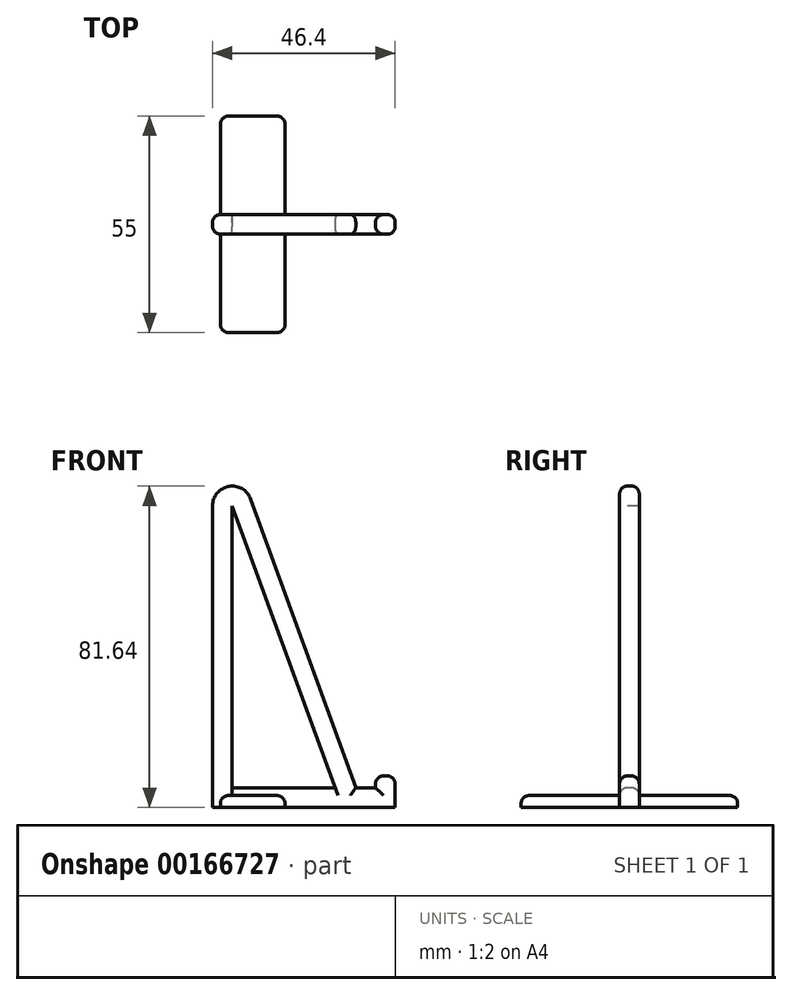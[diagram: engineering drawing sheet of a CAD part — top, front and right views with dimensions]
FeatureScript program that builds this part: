
annotation { "Feature Type Name" : "Feature", "Feature Type Description" : "" }
export const myFeature = defineFeature(function(context is Context, id is Id, definition is map)
    precondition{}
    {
        {
            var Q0;
            Q0=qCreatedBy(makeId("Front.planeOp"),FACE);
            var sketch = newSketch(context, id + "F0", { "sketchPlane" : qUnion([Q0])});
            skLineSegment(sketch, "E0", {"start": v(0, 0) * mm, "end": v(-46.4, 0) * mm});
            skLineSegment(sketch, "E1", {"start": v(-46.4, 0) * mm, "end": v(-46.4, 105) * mm});
            skLineSegment(sketch, "E2", {"start": v(-46.4, 105) * mm, "end": v(-10, 5) * mm});
            skLineSegment(sketch, "E3", {"start": v(-10, 5) * mm, "end": v(-5, 5) * mm});
            skLineSegment(sketch, "E4", {"start": v(-5, 5) * mm, "end": v(-5, 8) * mm});
            skLineSegment(sketch, "E5", {"start": v(-5, 8) * mm, "end": v(0, 8) * mm});
            skLineSegment(sketch, "E6", {"start": v(0, 8) * mm, "end": v(0, 0) * mm});
            skLineSegment(sketch, "E7", {"start": v(-41.4, 76.64) * mm, "end": v(-41.4, 5) * mm});
            skLineSegment(sketch, "E8", {"start": v(-41.4, 5) * mm, "end": v(-15.32, 5) * mm});
            skLineSegment(sketch, "E9", {"start": v(-15.32, 5) * mm, "end": v(-41.4, 76.64) * mm});
            skSolve(sketch);
        }
        {
            var Q0;
            Q0=makeQuery(id+"F0.imprint","IMPRINT",FACE,{"disambiguationData":[TD([[makeQuery(id+"F0.imprint","IMPRINT",EDGE,{"derivedFrom":sQuery(id+"F0.wireOp",EDGE,"E0")}),-1.0]])]});
            extrude(context, id + "F1", {"entities" : qUnion([Q0]), "oppositeDirection" : true, "depth" : 5 * mm});
        }
        {
            var Q0;
            Q0=makeQuery(id+"F1.opExtrude","SWEPT_FACE",FACE,{"disambiguationData":[OSD([sQuery(id+"F0.wireOp",EDGE,"E1")])]});
            var sketch = newSketch(context, id + "F2", { "sketchPlane" : qUnion([Q0])});
            skLineSegment(sketch, "E10.bottom", {"start": v(-5, 105) * mm, "end": v(0, 105) * mm});
            skLineSegment(sketch, "E10.top", {"start": v(-5, 5) * mm, "end": v(0, 5) * mm});
            skLineSegment(sketch, "E10.left", {"start": v(0, 105) * mm, "end": v(0, 5) * mm});
            skLineSegment(sketch, "E10.right", {"start": v(-5, 105) * mm, "end": v(-5, 5) * mm});
            skSolve(sketch);
        }
        {
            var Q0;
            Q0=makeQuery(id+"F9Pola5RWQbzexP_1.boolean.opBoolean","MERGE",FACE,{"derivedFrom":[makeQuery(id+"F1.opExtrude","SWEPT_FACE",FACE,{"disambiguationData":[OSD([sQuery(id+"F0.wireOp",EDGE,"E3")])]}),makeQuery(id+"F1.opExtrude","SWEPT_FACE",FACE,{"disambiguationData":[OSD([sQuery(id+"F0.wireOp",EDGE,"E8")])]}),makeQuery(id+"F9Pola5RWQbzexP_1.opExtrude","SWEPT_FACE",FACE,{"disambiguationData":[OSD([sQuery(id+"F2.wireOp",EDGE,"E10.top")])]})]});
            var sketch = newSketch(context, id + "F3", { "sketchPlane" : qUnion([Q0])});
            skLineSegment(sketch, "E11.bottom", {"start": v(0, 185) * mm, "end": v(-10, 185) * mm});
            skLineSegment(sketch, "E11.top", {"start": v(0, 5) * mm, "end": v(-10, 5) * mm});
            skLineSegment(sketch, "E11.left", {"start": v(0, 185) * mm, "end": v(0, 5) * mm});
            skLineSegment(sketch, "E11.right", {"start": v(-10, 185) * mm, "end": v(-10, 5) * mm});
            skSolve(sketch);
        }
        {
            var Q0;
            {var subQ0=sQuery(id+"F3.wireOp",EDGE,"E11.left");Q0=makeQuery(id+"F3.imprint","IMPRINT",FACE,{"disambiguationData":[TD([[makeQuery(id+"F3.imprint","IMPRINT",EDGE,{"derivedFrom":subQ0}),-1.0]])]});}
            extrude(context, id + "F4", {"entities" : qUnion([Q0]), "operationType" : NewBodyOperationType.REMOVE, "endBound" : BoundingType.THROUGH_ALL, "oppositeDirection" : true, "depth" : 25 * mm});
        }
        {
            var Q0;
            {var subQ0=sQuery(id+"F0.wireOp",EDGE,"E2");var subQ1=sQuery(id+"F0.wireOp",EDGE,"E1");Q0=makeQuery(id+"F9Pola5RWQbzexP_1.boolean.opBoolean","SPLIT",EDGE,{"disambiguationData":[TD([makeQuery(id+"F9Pola5RWQbzexP_1.opExtrude","SWEPT_FACE",FACE,{"disambiguationData":[OSD([sQuery(id+"F2.wireOp",EDGE,"E10.right")])]})])],"derivedFrom":makeQuery(id+"F1.opExtrude","SWEPT_EDGE",EDGE,{"disambiguationData":[OSD([subQ1,subQ0])]})});}
            var Q1;
            {var subQ0=sQuery(id+"F0.wireOp",EDGE,"E2");var subQ1=sQuery(id+"F0.wireOp",EDGE,"E1");Q1=makeQuery(id+"F9Pola5RWQbzexP_1.boolean.opBoolean","SPLIT",EDGE,{"disambiguationData":[TD([makeQuery(id+"F9Pola5RWQbzexP_1.opExtrude","SWEPT_FACE",FACE,{"disambiguationData":[OSD([sQuery(id+"F2.wireOp",EDGE,"E10.left")])]})])],"derivedFrom":makeQuery(id+"F1.opExtrude","SWEPT_EDGE",EDGE,{"disambiguationData":[OSD([subQ1,subQ0])]})});}
            fillet(context, id + "F5", {"entities" : qUnion([Q0, Q1]), "radius" : 5 * mm, "tangentPropagation" : true, "allowEdgeOverflow" : false});
        }
        {
            var Q0;
            {var subQ0=sQuery(id+"F0.wireOp",EDGE,"E9");var subQ1=sQuery(id+"F0.wireOp",EDGE,"E7");var subQ2=makeQuery(id+"F1.opExtrude","CAP_FACE",FACE,{"disambiguationData":[OSD([sQuery(id+"F0.wireOp",EDGE,"E0"),sQuery(id+"F0.wireOp",EDGE,"E1"),sQuery(id+"F0.wireOp",EDGE,"E2"),sQuery(id+"F0.wireOp",EDGE,"E3"),sQuery(id+"F0.wireOp",EDGE,"E4"),sQuery(id+"F0.wireOp",EDGE,"E5"),sQuery(id+"F0.wireOp",EDGE,"E6"),subQ1,sQuery(id+"F0.wireOp",EDGE,"E8"),subQ0])],"isStart":false});Q0=makeQuery(id+"F5.opFillet","BLEND_EDGE",EDGE,{"blendedFrom":[makeQuery(id+"F9Pola5RWQbzexP_1.boolean.opBoolean","SPLIT",EDGE,{"disambiguationData":[TD([makeQuery(id+"F9Pola5RWQbzexP_1.opExtrude","SWEPT_FACE",FACE,{"disambiguationData":[OSD([sQuery(id+"F2.wireOp",EDGE,"E10.left")])]})])],"derivedFrom":makeQuery(id+"F1.opExtrude","SWEPT_EDGE",EDGE,{"disambiguationData":[OSD([subQ1,subQ0])]})}),subQ2],"blendedInto":[subQ2]});}
            var Q1;
            {var subQ0=sQuery(id+"F0.wireOp",EDGE,"E2");var subQ1=sQuery(id+"F0.wireOp",EDGE,"E1");var subQ2=makeQuery(id+"F1.opExtrude","CAP_FACE",FACE,{"disambiguationData":[OSD([sQuery(id+"F0.wireOp",EDGE,"E0"),subQ1,subQ0,sQuery(id+"F0.wireOp",EDGE,"E3"),sQuery(id+"F0.wireOp",EDGE,"E4"),sQuery(id+"F0.wireOp",EDGE,"E5"),sQuery(id+"F0.wireOp",EDGE,"E6"),sQuery(id+"F0.wireOp",EDGE,"E7"),sQuery(id+"F0.wireOp",EDGE,"E8"),sQuery(id+"F0.wireOp",EDGE,"E9")])],"isStart":false});Q1=makeQuery(id+"F5.opFillet","BLEND_EDGE",EDGE,{"blendedFrom":[makeQuery(id+"F9Pola5RWQbzexP_1.boolean.opBoolean","SPLIT",EDGE,{"disambiguationData":[TD([makeQuery(id+"F9Pola5RWQbzexP_1.opExtrude","SWEPT_FACE",FACE,{"disambiguationData":[OSD([sQuery(id+"F2.wireOp",EDGE,"E10.left")])]})])],"derivedFrom":makeQuery(id+"F1.opExtrude","SWEPT_EDGE",EDGE,{"disambiguationData":[OSD([subQ1,subQ0])]})}),subQ2],"blendedInto":[subQ2]});}
            var Q2;
            {var subQ2=sQuery(id+"F0.wireOp",EDGE,"E7");var subQ4=sQuery(id+"F0.wireOp",EDGE,"E1");var subQ6=sQuery(id+"F0.wireOp",EDGE,"E9");var subQ8=makeQuery(id+"F9Pola5RWQbzexP_1.opExtrude","SWEPT_FACE",FACE,{"disambiguationData":[OSD([sQuery(id+"F2.wireOp",EDGE,"E10.right")])]});Q2=makeQuery(id+"F5.opFillet","BLEND_EDGE",EDGE,{"blendedFrom":[makeQuery(id+"F9Pola5RWQbzexP_1.boolean.opBoolean","SPLIT",EDGE,{"disambiguationData":[TD([subQ8])],"derivedFrom":makeQuery(id+"F1.opExtrude","SWEPT_EDGE",EDGE,{"disambiguationData":[OSD([subQ2,subQ6])]})}),makeQuery(id+"F9Pola5RWQbzexP_1.boolean.opBoolean","COPY",FACE,{"disambiguationData":[TD([makeQuery(id+"F1.opExtrude","SWEPT_FACE",FACE,{"disambiguationData":[OSD([subQ4])]})])],"derivedFrom":subQ8})],"blendedInto":[makeQuery(id+"F9Pola5RWQbzexP_1.boolean.opBoolean","COPY",FACE,{"disambiguationData":[TD([makeQuery(id+"F1.opExtrude","SWEPT_FACE",FACE,{"disambiguationData":[OSD([subQ4])]})])],"derivedFrom":subQ8})]});}
            var Q3;
            {var subQ1=sQuery(id+"F0.wireOp",EDGE,"E2");var subQ4=sQuery(id+"F0.wireOp",EDGE,"E1");var subQ5=makeQuery(id+"F1.opExtrude","SWEPT_FACE",FACE,{"disambiguationData":[OSD([subQ4])]});var subQ8=makeQuery(id+"F9Pola5RWQbzexP_1.opExtrude","SWEPT_FACE",FACE,{"disambiguationData":[OSD([sQuery(id+"F2.wireOp",EDGE,"E10.right")])]});Q3=makeQuery(id+"F5.opFillet","BLEND_EDGE",EDGE,{"blendedFrom":[makeQuery(id+"F9Pola5RWQbzexP_1.boolean.opBoolean","SPLIT",EDGE,{"disambiguationData":[TD([subQ8])],"derivedFrom":makeQuery(id+"F1.opExtrude","SWEPT_EDGE",EDGE,{"disambiguationData":[OSD([subQ4,subQ1])]})}),makeQuery(id+"F9Pola5RWQbzexP_1.boolean.opBoolean","COPY",FACE,{"disambiguationData":[TD([subQ5])],"derivedFrom":subQ8})],"blendedInto":[makeQuery(id+"F9Pola5RWQbzexP_1.boolean.opBoolean","COPY",FACE,{"disambiguationData":[TD([subQ5])],"derivedFrom":subQ8})]});}
            var Q4;
            {var subQ0=sQuery(id+"F0.wireOp",EDGE,"E9");var subQ1=sQuery(id+"F0.wireOp",EDGE,"E7");var subQ2=makeQuery(id+"F1.opExtrude","CAP_FACE",FACE,{"disambiguationData":[OSD([sQuery(id+"F0.wireOp",EDGE,"E0"),sQuery(id+"F0.wireOp",EDGE,"E1"),sQuery(id+"F0.wireOp",EDGE,"E2"),sQuery(id+"F0.wireOp",EDGE,"E3"),sQuery(id+"F0.wireOp",EDGE,"E4"),sQuery(id+"F0.wireOp",EDGE,"E5"),sQuery(id+"F0.wireOp",EDGE,"E6"),subQ1,sQuery(id+"F0.wireOp",EDGE,"E8"),subQ0])],"isStart":true});Q4=makeQuery(id+"F5.opFillet","BLEND_EDGE",EDGE,{"blendedFrom":[makeQuery(id+"F9Pola5RWQbzexP_1.boolean.opBoolean","SPLIT",EDGE,{"disambiguationData":[TD([makeQuery(id+"F9Pola5RWQbzexP_1.opExtrude","SWEPT_FACE",FACE,{"disambiguationData":[OSD([sQuery(id+"F2.wireOp",EDGE,"E10.right")])]})])],"derivedFrom":makeQuery(id+"F1.opExtrude","SWEPT_EDGE",EDGE,{"disambiguationData":[OSD([subQ1,subQ0])]})}),subQ2],"blendedInto":[subQ2]});}
            var Q5;
            {var subQ0=sQuery(id+"F0.wireOp",EDGE,"E2");var subQ1=sQuery(id+"F0.wireOp",EDGE,"E1");var subQ2=makeQuery(id+"F1.opExtrude","CAP_FACE",FACE,{"disambiguationData":[OSD([sQuery(id+"F0.wireOp",EDGE,"E0"),subQ1,subQ0,sQuery(id+"F0.wireOp",EDGE,"E3"),sQuery(id+"F0.wireOp",EDGE,"E4"),sQuery(id+"F0.wireOp",EDGE,"E5"),sQuery(id+"F0.wireOp",EDGE,"E6"),sQuery(id+"F0.wireOp",EDGE,"E7"),sQuery(id+"F0.wireOp",EDGE,"E8"),sQuery(id+"F0.wireOp",EDGE,"E9")])],"isStart":true});Q5=makeQuery(id+"F5.opFillet","BLEND_EDGE",EDGE,{"blendedFrom":[makeQuery(id+"F9Pola5RWQbzexP_1.boolean.opBoolean","SPLIT",EDGE,{"disambiguationData":[TD([makeQuery(id+"F9Pola5RWQbzexP_1.opExtrude","SWEPT_FACE",FACE,{"disambiguationData":[OSD([sQuery(id+"F2.wireOp",EDGE,"E10.right")])]})])],"derivedFrom":makeQuery(id+"F1.opExtrude","SWEPT_EDGE",EDGE,{"disambiguationData":[OSD([subQ1,subQ0])]})}),subQ2],"blendedInto":[subQ2]});}
            var Q6;
            {var subQ2=sQuery(id+"F0.wireOp",EDGE,"E7");var subQ4=sQuery(id+"F0.wireOp",EDGE,"E1");var subQ6=sQuery(id+"F0.wireOp",EDGE,"E9");var subQ8=makeQuery(id+"F9Pola5RWQbzexP_1.opExtrude","SWEPT_FACE",FACE,{"disambiguationData":[OSD([sQuery(id+"F2.wireOp",EDGE,"E10.left")])]});Q6=makeQuery(id+"F5.opFillet","BLEND_EDGE",EDGE,{"blendedFrom":[makeQuery(id+"F9Pola5RWQbzexP_1.boolean.opBoolean","SPLIT",EDGE,{"disambiguationData":[TD([subQ8])],"derivedFrom":makeQuery(id+"F1.opExtrude","SWEPT_EDGE",EDGE,{"disambiguationData":[OSD([subQ2,subQ6])]})}),makeQuery(id+"F9Pola5RWQbzexP_1.boolean.opBoolean","COPY",FACE,{"disambiguationData":[TD([makeQuery(id+"F1.opExtrude","SWEPT_FACE",FACE,{"disambiguationData":[OSD([subQ4])]})])],"derivedFrom":subQ8})],"blendedInto":[makeQuery(id+"F9Pola5RWQbzexP_1.boolean.opBoolean","COPY",FACE,{"disambiguationData":[TD([makeQuery(id+"F1.opExtrude","SWEPT_FACE",FACE,{"disambiguationData":[OSD([subQ4])]})])],"derivedFrom":subQ8})]});}
            var Q7;
            {var subQ1=sQuery(id+"F0.wireOp",EDGE,"E2");var subQ4=sQuery(id+"F0.wireOp",EDGE,"E1");var subQ5=makeQuery(id+"F1.opExtrude","SWEPT_FACE",FACE,{"disambiguationData":[OSD([subQ4])]});var subQ8=makeQuery(id+"F9Pola5RWQbzexP_1.opExtrude","SWEPT_FACE",FACE,{"disambiguationData":[OSD([sQuery(id+"F2.wireOp",EDGE,"E10.left")])]});Q7=makeQuery(id+"F5.opFillet","BLEND_EDGE",EDGE,{"blendedFrom":[makeQuery(id+"F9Pola5RWQbzexP_1.boolean.opBoolean","SPLIT",EDGE,{"disambiguationData":[TD([subQ8])],"derivedFrom":makeQuery(id+"F1.opExtrude","SWEPT_EDGE",EDGE,{"disambiguationData":[OSD([subQ4,subQ1])]})}),makeQuery(id+"F9Pola5RWQbzexP_1.boolean.opBoolean","COPY",FACE,{"disambiguationData":[TD([subQ5])],"derivedFrom":subQ8})],"blendedInto":[makeQuery(id+"F9Pola5RWQbzexP_1.boolean.opBoolean","COPY",FACE,{"disambiguationData":[TD([subQ5])],"derivedFrom":subQ8})]});}
            fillet(context, id + "F6", {"entities" : qUnion([Q0, Q1, Q2, Q3, Q4, Q5, Q6, Q7]), "radius" : 2 * mm, "tangentPropagation" : true, "allowEdgeOverflow" : false});
        }
        {
            var Q0;
            Q0=makeQuery(id+"F4.boolean.opBoolean","COPY",EDGE,{"derivedFrom":makeQuery(id+"F4.opExtrude","CAP_EDGE",EDGE,{"disambiguationData":[OSD([sQuery(id+"F3.wireOp",EDGE,"E11.right")])],"isStart":true})});
            var Q1;
            Q1=makeQuery(id+"F9Pola5RWQbzexP_1.boolean.opBoolean","COPY",EDGE,{"derivedFrom":makeQuery(id+"F9Pola5RWQbzexP_1.opExtrude","CAP_EDGE",EDGE,{"disambiguationData":[OSD([sQuery(id+"F2.wireOp",EDGE,"E10.top")])],"isStart":true})});
            var Q2;
            Q2=makeQuery(id+"F1.opExtrude","CAP_EDGE",EDGE,{"disambiguationData":[OSD([sQuery(id+"F0.wireOp",EDGE,"E8")])],"isStart":true});
            var Q3;
            Q3=makeQuery(id+"F1.opExtrude","CAP_EDGE",EDGE,{"disambiguationData":[OSD([sQuery(id+"F0.wireOp",EDGE,"E8")])],"isStart":false});
            fillet(context, id + "F7", {"entities" : qUnion([Q0, Q1, Q2, Q3]), "radius" : 2 * mm, "tangentPropagation" : true, "allowEdgeOverflow" : false});
        }
        {
            var Q0;
            {var subQ0=sQuery(id+"F0.wireOp",EDGE,"E6");var subQ1=sQuery(id+"F0.wireOp",EDGE,"E5");Q0=makeQuery(id+"F9Pola5RWQbzexP_1.boolean.opBoolean","SPLIT",EDGE,{"disambiguationData":[TD([makeQuery(id+"F9Pola5RWQbzexP_1.opExtrude","SWEPT_FACE",FACE,{"disambiguationData":[OSD([sQuery(id+"F2.wireOp",EDGE,"E10.right")])]})])],"derivedFrom":makeQuery(id+"F1.opExtrude","SWEPT_EDGE",EDGE,{"disambiguationData":[OSD([subQ1,subQ0])]})});}
            var Q1;
            Q1=makeQuery(id+"F9Pola5RWQbzexP_1.boolean.opBoolean","INTERSECT",EDGE,{"derivedFrom":[makeQuery(id+"F1.opExtrude","SWEPT_FACE",FACE,{"disambiguationData":[OSD([sQuery(id+"F0.wireOp",EDGE,"E5")])]}),makeQuery(id+"F9Pola5RWQbzexP_1.opExtrude","SWEPT_FACE",FACE,{"disambiguationData":[OSD([sQuery(id+"F2.wireOp",EDGE,"E10.right")])]})]});
            var Q2;
            Q2=makeQuery(id+"F1.opExtrude","CAP_EDGE",EDGE,{"disambiguationData":[OSD([sQuery(id+"F0.wireOp",EDGE,"E5")])],"isStart":true});
            var Q3;
            {var subQ0=sQuery(id+"F0.wireOp",EDGE,"E5");var subQ1=sQuery(id+"F0.wireOp",EDGE,"E4");Q3=makeQuery(id+"F9Pola5RWQbzexP_1.boolean.opBoolean","SPLIT",EDGE,{"disambiguationData":[TD([makeQuery(id+"F9Pola5RWQbzexP_1.opExtrude","SWEPT_FACE",FACE,{"disambiguationData":[OSD([sQuery(id+"F2.wireOp",EDGE,"E10.right")])]})])],"derivedFrom":makeQuery(id+"F1.opExtrude","SWEPT_EDGE",EDGE,{"disambiguationData":[OSD([subQ1,subQ0])]})});}
            var Q4;
            Q4=makeQuery(id+"F1.opExtrude","CAP_EDGE",EDGE,{"disambiguationData":[OSD([sQuery(id+"F0.wireOp",EDGE,"E4")])],"isStart":true});
            var Q5;
            Q5=makeQuery(id+"F1.opExtrude","CAP_EDGE",EDGE,{"disambiguationData":[OSD([sQuery(id+"F0.wireOp",EDGE,"E6")])],"isStart":true});
            var Q6;
            Q6=makeQuery(id+"F4.boolean.opBoolean","MERGE",EDGE,{"derivedFrom":[makeQuery(id+"F9Pola5RWQbzexP_1.boolean.opBoolean","INTERSECT",EDGE,{"derivedFrom":[makeQuery(id+"F1.opExtrude","SWEPT_FACE",FACE,{"disambiguationData":[OSD([sQuery(id+"F0.wireOp",EDGE,"E6")])]}),makeQuery(id+"F9Pola5RWQbzexP_1.opExtrude","SWEPT_FACE",FACE,{"disambiguationData":[OSD([sQuery(id+"F2.wireOp",EDGE,"E10.right")])]})]}),makeQuery(id+"F4.opExtrude","SWEPT_EDGE",EDGE,{"disambiguationData":[OSD([sQuery(id+"F3.wireOp",EDGE,"E11.top"),sQuery(id+"F3.wireOp",EDGE,"E11.left")])]})]});
            var Q7;
            Q7=makeQuery(id+"F9Pola5RWQbzexP_1.boolean.opBoolean","INTERSECT",EDGE,{"derivedFrom":[makeQuery(id+"F1.opExtrude","SWEPT_FACE",FACE,{"disambiguationData":[OSD([sQuery(id+"F0.wireOp",EDGE,"E4")])]}),makeQuery(id+"F9Pola5RWQbzexP_1.opExtrude","SWEPT_FACE",FACE,{"disambiguationData":[OSD([sQuery(id+"F2.wireOp",EDGE,"E10.right")])]})]});
            var Q8;
            Q8=makeQuery(id+"F4.boolean.opBoolean","COPY",EDGE,{"derivedFrom":makeQuery(id+"F4.opExtrude","CAP_EDGE",EDGE,{"disambiguationData":[OSD([sQuery(id+"F3.wireOp",EDGE,"E11.top")])],"isStart":true})});
            var Q9;
            Q9=makeQuery(id+"F1.opExtrude","CAP_EDGE",EDGE,{"disambiguationData":[OSD([sQuery(id+"F0.wireOp",EDGE,"E3")])],"isStart":true});
            fillet(context, id + "F8", {"entities" : qUnion([Q0, Q1, Q2, Q3, Q4, Q5, Q6, Q7, Q8, Q9]), "radius" : 2 * mm, "tangentPropagation" : true, "allowEdgeOverflow" : false});
        }
        {
            var Q0;
            {var subQ0=sQuery(id+"F0.wireOp",EDGE,"E6");var subQ1=sQuery(id+"F0.wireOp",EDGE,"E5");Q0=makeQuery(id+"F9Pola5RWQbzexP_1.boolean.opBoolean","SPLIT",EDGE,{"disambiguationData":[TD([makeQuery(id+"F9Pola5RWQbzexP_1.opExtrude","SWEPT_FACE",FACE,{"disambiguationData":[OSD([sQuery(id+"F2.wireOp",EDGE,"E10.left")])]})])],"derivedFrom":makeQuery(id+"F1.opExtrude","SWEPT_EDGE",EDGE,{"disambiguationData":[OSD([subQ1,subQ0])]})});}
            var Q1;
            Q1=makeQuery(id+"F9Pola5RWQbzexP_1.boolean.opBoolean","INTERSECT",EDGE,{"derivedFrom":[makeQuery(id+"F1.opExtrude","SWEPT_FACE",FACE,{"disambiguationData":[OSD([sQuery(id+"F0.wireOp",EDGE,"E5")])]}),makeQuery(id+"F9Pola5RWQbzexP_1.opExtrude","SWEPT_FACE",FACE,{"disambiguationData":[OSD([sQuery(id+"F2.wireOp",EDGE,"E10.left")])]})]});
            var Q2;
            {var subQ0=sQuery(id+"F0.wireOp",EDGE,"E5");var subQ1=sQuery(id+"F0.wireOp",EDGE,"E4");Q2=makeQuery(id+"F9Pola5RWQbzexP_1.boolean.opBoolean","SPLIT",EDGE,{"disambiguationData":[TD([makeQuery(id+"F9Pola5RWQbzexP_1.opExtrude","SWEPT_FACE",FACE,{"disambiguationData":[OSD([sQuery(id+"F2.wireOp",EDGE,"E10.left")])]})])],"derivedFrom":makeQuery(id+"F1.opExtrude","SWEPT_EDGE",EDGE,{"disambiguationData":[OSD([subQ1,subQ0])]})});}
            var Q3;
            Q3=makeQuery(id+"F1.opExtrude","CAP_EDGE",EDGE,{"disambiguationData":[OSD([sQuery(id+"F0.wireOp",EDGE,"E5")])],"isStart":false});
            var Q4;
            Q4=makeQuery(id+"F4.boolean.opBoolean","MERGE",EDGE,{"derivedFrom":[makeQuery(id+"F9Pola5RWQbzexP_1.boolean.opBoolean","INTERSECT",EDGE,{"derivedFrom":[makeQuery(id+"F1.opExtrude","SWEPT_FACE",FACE,{"disambiguationData":[OSD([sQuery(id+"F0.wireOp",EDGE,"E6")])]}),makeQuery(id+"F9Pola5RWQbzexP_1.opExtrude","SWEPT_FACE",FACE,{"disambiguationData":[OSD([sQuery(id+"F2.wireOp",EDGE,"E10.left")])]})]}),makeQuery(id+"F4.opExtrude","SWEPT_EDGE",EDGE,{"disambiguationData":[OSD([sQuery(id+"F3.wireOp",EDGE,"E11.bottom"),sQuery(id+"F3.wireOp",EDGE,"E11.left")])]})]});
            var Q5;
            Q5=makeQuery(id+"F1.opExtrude","CAP_EDGE",EDGE,{"disambiguationData":[OSD([sQuery(id+"F0.wireOp",EDGE,"E6")])],"isStart":false});
            var Q6;
            Q6=makeQuery(id+"F9Pola5RWQbzexP_1.boolean.opBoolean","INTERSECT",EDGE,{"derivedFrom":[makeQuery(id+"F1.opExtrude","SWEPT_FACE",FACE,{"disambiguationData":[OSD([sQuery(id+"F0.wireOp",EDGE,"E4")])]}),makeQuery(id+"F9Pola5RWQbzexP_1.opExtrude","SWEPT_FACE",FACE,{"disambiguationData":[OSD([sQuery(id+"F2.wireOp",EDGE,"E10.left")])]})]});
            var Q7;
            Q7=makeQuery(id+"F4.boolean.opBoolean","COPY",EDGE,{"derivedFrom":makeQuery(id+"F4.opExtrude","CAP_EDGE",EDGE,{"disambiguationData":[OSD([sQuery(id+"F3.wireOp",EDGE,"E11.bottom")])],"isStart":true})});
            var Q8;
            Q8=makeQuery(id+"F1.opExtrude","CAP_EDGE",EDGE,{"disambiguationData":[OSD([sQuery(id+"F0.wireOp",EDGE,"E4")])],"isStart":false});
            var Q9;
            Q9=makeQuery(id+"F1.opExtrude","CAP_EDGE",EDGE,{"disambiguationData":[OSD([sQuery(id+"F0.wireOp",EDGE,"E3")])],"isStart":false});
            fillet(context, id + "F9", {"entities" : qUnion([Q0, Q1, Q2, Q3, Q4, Q5, Q6, Q7, Q8, Q9]), "radius" : 2 * mm, "tangentPropagation" : true, "allowEdgeOverflow" : false});
        }
        {
            var Q0;
            Q0=makeQuery(id+"F1.opExtrude","CAP_FACE",FACE,{"disambiguationData":[OSD([sQuery(id+"F0.wireOp",EDGE,"E0"),sQuery(id+"F0.wireOp",EDGE,"E1"),sQuery(id+"F0.wireOp",EDGE,"E2"),sQuery(id+"F0.wireOp",EDGE,"E3"),sQuery(id+"F0.wireOp",EDGE,"E4"),sQuery(id+"F0.wireOp",EDGE,"E5"),sQuery(id+"F0.wireOp",EDGE,"E6"),sQuery(id+"F0.wireOp",EDGE,"E7"),sQuery(id+"F0.wireOp",EDGE,"E8"),sQuery(id+"F0.wireOp",EDGE,"E9")])],"isStart":true});
            var sketch = newSketch(context, id + "F10", { "sketchPlane" : qUnion([Q0])});
            skLineSegment(sketch, "E12.bottom", {"start": v(-44.4, 0) * mm, "end": v(-28, 0) * mm});
            skLineSegment(sketch, "E12.top", {"start": v(-44.4, 3) * mm, "end": v(-28, 3) * mm});
            skLineSegment(sketch, "E12.left", {"start": v(-44.4, 0) * mm, "end": v(-44.4, 3) * mm});
            skLineSegment(sketch, "E12.right", {"start": v(-28, 0) * mm, "end": v(-28, 3) * mm});
            skSolve(sketch);
        }
        {
            var Q0;
            Q0=makeQuery(id+"F10.imprint","IMPRINT",FACE,{"disambiguationData":[TD([[makeQuery(id+"F10.imprint","IMPRINT",EDGE,{"derivedFrom":sQuery(id+"F10.wireOp",EDGE,"E12.bottom")}),-1.0]])]});
            extrude(context, id + "F11", {"entities" : qUnion([Q0]), "operationType" : NewBodyOperationType.ADD, "depth" : 25 * mm});
        }
        {
            var Q0;
            Q0=makeQuery(id+"F1.opExtrude","CAP_FACE",FACE,{"disambiguationData":[OSD([sQuery(id+"F0.wireOp",EDGE,"E0"),sQuery(id+"F0.wireOp",EDGE,"E1"),sQuery(id+"F0.wireOp",EDGE,"E2"),sQuery(id+"F0.wireOp",EDGE,"E3"),sQuery(id+"F0.wireOp",EDGE,"E4"),sQuery(id+"F0.wireOp",EDGE,"E5"),sQuery(id+"F0.wireOp",EDGE,"E6"),sQuery(id+"F0.wireOp",EDGE,"E7"),sQuery(id+"F0.wireOp",EDGE,"E8"),sQuery(id+"F0.wireOp",EDGE,"E9")])],"isStart":false});
            var sketch = newSketch(context, id + "F12", { "sketchPlane" : qUnion([Q0])});
            skLineSegment(sketch, "E13.bottom", {"start": v(44.4, 0) * mm, "end": v(28, 0) * mm});
            skLineSegment(sketch, "E13.top", {"start": v(44.4, 3) * mm, "end": v(28, 3) * mm});
            skLineSegment(sketch, "E13.left", {"start": v(44.4, 0) * mm, "end": v(44.4, 3) * mm});
            skLineSegment(sketch, "E13.right", {"start": v(28, 0) * mm, "end": v(28, 3) * mm});
            skSolve(sketch);
        }
        {
            var Q0;
            Q0=makeQuery(id+"F12.imprint","IMPRINT",FACE,{"disambiguationData":[TD([[makeQuery(id+"F12.imprint","IMPRINT",EDGE,{"derivedFrom":sQuery(id+"F12.wireOp",EDGE,"E13.bottom")}),1.0]])]});
            extrude(context, id + "F13", {"entities" : qUnion([Q0]), "operationType" : NewBodyOperationType.ADD, "depth" : 25 * mm});
        }
        {
            var Q0;
            Q0=makeQuery(id+"F11.opExtrude","CAP_EDGE",EDGE,{"disambiguationData":[OSD([sQuery(id+"F10.wireOp",EDGE,"E12.right")])],"isStart":false});
            var Q1;
            Q1=makeQuery(id+"F11.opExtrude","CAP_EDGE",EDGE,{"disambiguationData":[OSD([sQuery(id+"F10.wireOp",EDGE,"E12.left")])],"isStart":false});
            var Q2;
            Q2=makeQuery(id+"F11.opExtrude","CAP_EDGE",EDGE,{"disambiguationData":[OSD([sQuery(id+"F10.wireOp",EDGE,"E12.top")])],"isStart":false});
            var Q3;
            Q3=makeQuery(id+"F11.opExtrude","SWEPT_EDGE",EDGE,{"disambiguationData":[OSD([sQuery(id+"F0.wireOp",EDGE,"E0"),sQuery(id+"F0.wireOp",EDGE,"E1"),sQuery(id+"F0.wireOp",EDGE,"E2"),sQuery(id+"F0.wireOp",EDGE,"E3"),sQuery(id+"F0.wireOp",EDGE,"E4"),sQuery(id+"F0.wireOp",EDGE,"E5"),sQuery(id+"F0.wireOp",EDGE,"E6"),sQuery(id+"F0.wireOp",EDGE,"E7"),sQuery(id+"F0.wireOp",EDGE,"E8"),sQuery(id+"F0.wireOp",EDGE,"E9"),sQuery(id+"F10.wireOp",EDGE,"E12.top"),sQuery(id+"F10.wireOp",EDGE,"E12.right")])]});
            var Q4;
            Q4=makeQuery(id+"F11.opExtrude","SWEPT_EDGE",EDGE,{"disambiguationData":[OSD([sQuery(id+"F0.wireOp",EDGE,"E0"),sQuery(id+"F0.wireOp",EDGE,"E1"),sQuery(id+"F0.wireOp",EDGE,"E2"),sQuery(id+"F0.wireOp",EDGE,"E3"),sQuery(id+"F0.wireOp",EDGE,"E4"),sQuery(id+"F0.wireOp",EDGE,"E5"),sQuery(id+"F0.wireOp",EDGE,"E6"),sQuery(id+"F0.wireOp",EDGE,"E7"),sQuery(id+"F0.wireOp",EDGE,"E8"),sQuery(id+"F0.wireOp",EDGE,"E9"),sQuery(id+"F10.wireOp",EDGE,"E12.top"),sQuery(id+"F10.wireOp",EDGE,"E12.left")])]});
            var Q5;
            Q5=makeQuery(id+"F13.opExtrude","CAP_EDGE",EDGE,{"disambiguationData":[OSD([sQuery(id+"F12.wireOp",EDGE,"E13.right")])],"isStart":false});
            var Q6;
            Q6=makeQuery(id+"F13.opExtrude","CAP_EDGE",EDGE,{"disambiguationData":[OSD([sQuery(id+"F12.wireOp",EDGE,"E13.left")])],"isStart":false});
            var Q7;
            Q7=makeQuery(id+"F13.opExtrude","SWEPT_EDGE",EDGE,{"disambiguationData":[OSD([sQuery(id+"F0.wireOp",EDGE,"E0"),sQuery(id+"F0.wireOp",EDGE,"E1"),sQuery(id+"F0.wireOp",EDGE,"E2"),sQuery(id+"F0.wireOp",EDGE,"E3"),sQuery(id+"F0.wireOp",EDGE,"E4"),sQuery(id+"F0.wireOp",EDGE,"E5"),sQuery(id+"F0.wireOp",EDGE,"E6"),sQuery(id+"F0.wireOp",EDGE,"E7"),sQuery(id+"F0.wireOp",EDGE,"E8"),sQuery(id+"F0.wireOp",EDGE,"E9"),sQuery(id+"F12.wireOp",EDGE,"E13.top"),sQuery(id+"F12.wireOp",EDGE,"E13.right")])]});
            var Q8;
            Q8=makeQuery(id+"F13.opExtrude","CAP_EDGE",EDGE,{"disambiguationData":[OSD([sQuery(id+"F12.wireOp",EDGE,"E13.top")])],"isStart":false});
            var Q9;
            Q9=makeQuery(id+"F13.opExtrude","SWEPT_EDGE",EDGE,{"disambiguationData":[OSD([sQuery(id+"F0.wireOp",EDGE,"E0"),sQuery(id+"F0.wireOp",EDGE,"E1"),sQuery(id+"F0.wireOp",EDGE,"E2"),sQuery(id+"F0.wireOp",EDGE,"E3"),sQuery(id+"F0.wireOp",EDGE,"E4"),sQuery(id+"F0.wireOp",EDGE,"E5"),sQuery(id+"F0.wireOp",EDGE,"E6"),sQuery(id+"F0.wireOp",EDGE,"E7"),sQuery(id+"F0.wireOp",EDGE,"E8"),sQuery(id+"F0.wireOp",EDGE,"E9"),sQuery(id+"F12.wireOp",EDGE,"E13.top"),sQuery(id+"F12.wireOp",EDGE,"E13.left")])]});
            fillet(context, id + "F14", {"entities" : qUnion([Q0, Q1, Q2, Q3, Q4, Q5, Q6, Q7, Q8, Q9]), "radius" : 2 * mm, "tangentPropagation" : true, "allowEdgeOverflow" : false});
        }
    });
